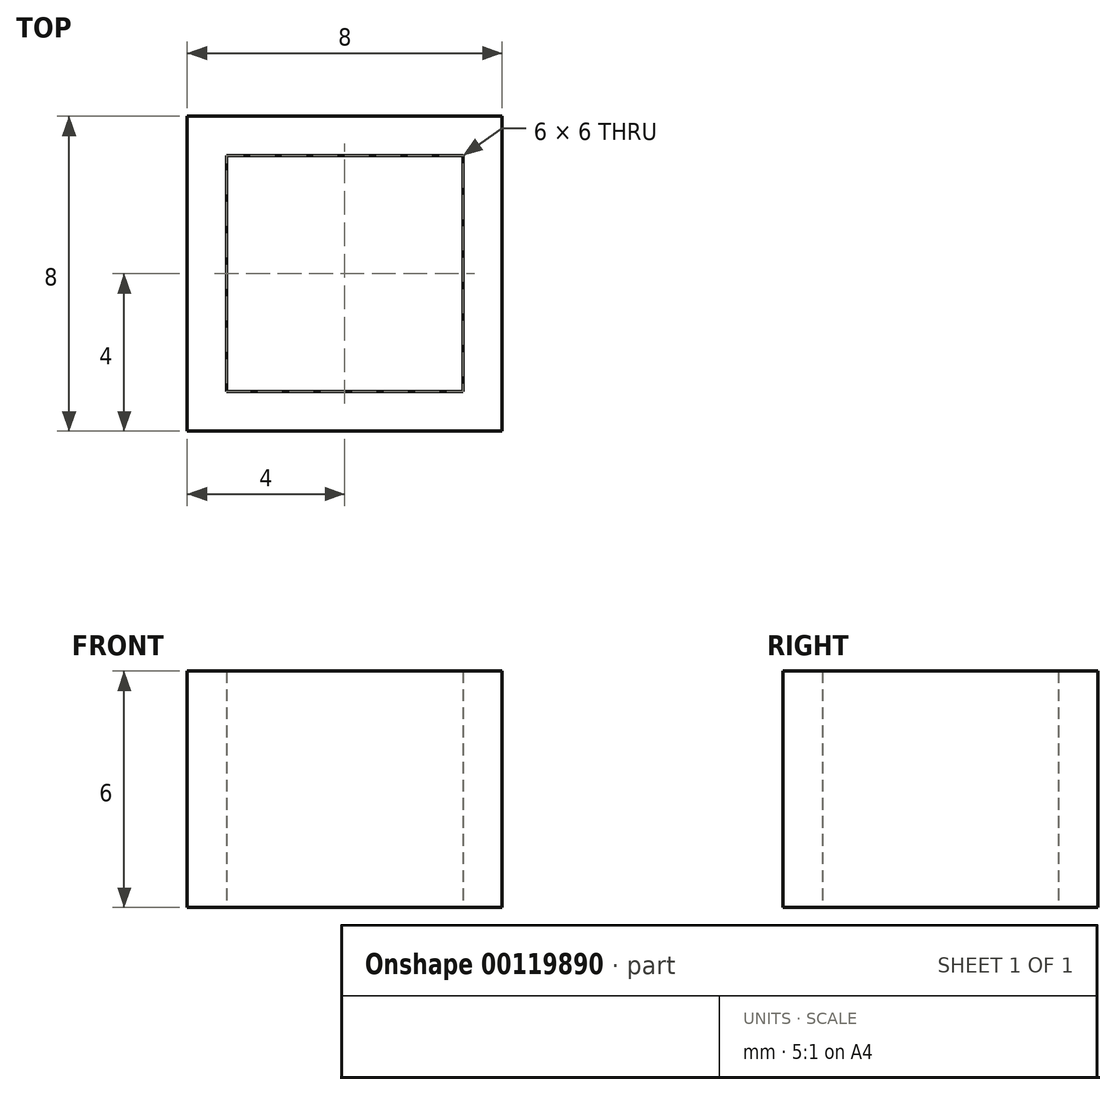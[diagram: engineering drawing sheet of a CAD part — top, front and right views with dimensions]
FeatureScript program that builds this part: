
annotation { "Feature Type Name" : "Feature", "Feature Type Description" : "" }
export const myFeature = defineFeature(function(context is Context, id is Id, definition is map)
    precondition{}
    {
        {
            assignVariable(context, id + "F0", {"name" : "cubeSide", "anyValue" : 6});
        }
        {
            var Q0;
            Q0=qCreatedBy(makeId("Top.planeOp"),FACE);
            var sketch = newSketch(context, id + "F1", { "sketchPlane" : qUnion([Q0])});
            skLineSegment(sketch, "E0.bottom", {"start": v(4, -3.5) * mm, "end": v(-4, -3.5) * mm});
            skLineSegment(sketch, "E0.left", {"start": v(4, -3.5) * mm, "end": v(4, 3.5) * mm});
            skLineSegment(sketch, "E0.right", {"start": v(-4, -3.5) * mm, "end": v(-4, 3.5) * mm});
            skPoint(sketch, "E0.middle", {"position": v(0, 0) * mm});
            skLineSegment(sketch, "E1.top", {"start": v(-3, -2.5) * mm, "end": v(3, -2.5) * mm});
            skLineSegment(sketch, "E1.left", {"start": v(-3, 3.5) * mm, "end": v(-3, -2.5) * mm});
            skLineSegment(sketch, "E1.right", {"start": v(3, 3.5) * mm, "end": v(3, -2.5) * mm});
            skLineSegment(sketch, "E2.bottom", {"start": v(-3, 3.5) * mm, "end": v(3, 3.5) * mm});
            skLineSegment(sketch, "E2.top", {"start": v(-4, 4.5) * mm, "end": v(4, 4.5) * mm});
            skLineSegment(sketch, "E2.left", {"start": v(-4, 3.5) * mm, "end": v(-4, 4.5) * mm});
            skLineSegment(sketch, "E2.right", {"start": v(4, 3.5) * mm, "end": v(4, 4.5) * mm});
            skSolve(sketch);
        }
        {
            var Q0;
            Q0=makeQuery(id+"F1.imprint","IMPRINT",FACE,{"disambiguationData":[TD([[makeQuery(id+"F1.imprint","IMPRINT",EDGE,{"derivedFrom":sQuery(id+"F1.wireOp",EDGE,"E0.bottom")}),-1.0]])]});
            extrude(context, id + "F2", {"entities" : qUnion([Q0]), "depth" : (getVariable(context, 'cubeSide')) * mm});
        }
    });
